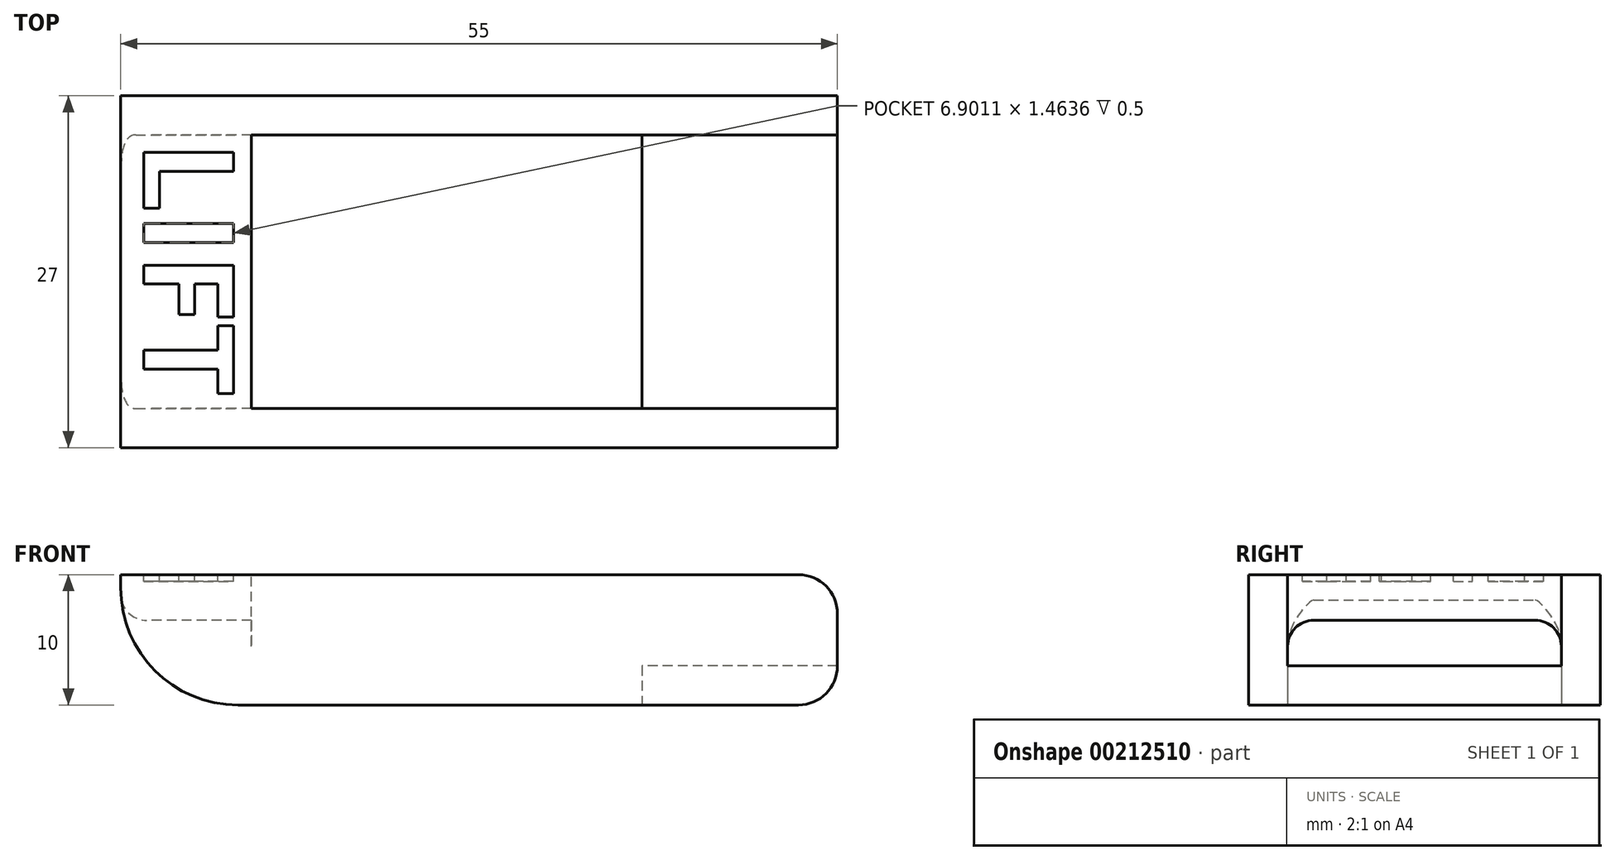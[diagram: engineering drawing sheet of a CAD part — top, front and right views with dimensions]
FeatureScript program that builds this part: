
annotation { "Feature Type Name" : "Feature", "Feature Type Description" : "" }
export const myFeature = defineFeature(function(context is Context, id is Id, definition is map)
    precondition{}
    {
        {
            var Q0;
            Q0=qCreatedBy(makeId("Top.planeOp"),FACE);
            var sketch = newSketch(context, id + "F0", { "sketchPlane" : qUnion([Q0])});
            skLineSegment(sketch, "E0.bottom", {"start": v(27.5, -10.5) * mm, "end": v(-27.5, -10.5) * mm});
            skLineSegment(sketch, "E0.top", {"start": v(27.5, 10.5) * mm, "end": v(-27.5, 10.5) * mm});
            skLineSegment(sketch, "E0.left", {"start": v(27.5, -10.5) * mm, "end": v(27.5, 10.5) * mm});
            skLineSegment(sketch, "E0.right", {"start": v(-27.5, -10.5) * mm, "end": v(-27.5, 10.5) * mm});
            skPoint(sketch, "E0.middle", {"position": v(0, 0) * mm});
            skLineSegment(sketch, "E1", {"start": v(12.5, 10.5) * mm, "end": v(12.5, -10.5) * mm});
            skLineSegment(sketch, "E2", {"start": v(27.5, 10.5) * mm, "end": v(27.5, 13.5) * mm});
            skLineSegment(sketch, "E3", {"start": v(27.5, 13.5) * mm, "end": v(-27.5, 13.5) * mm});
            skLineSegment(sketch, "E4", {"start": v(-27.5, 13.5) * mm, "end": v(-27.5, 10.5) * mm});
            skLineSegment(sketch, "E5", {"start": v(27.5, -10.5) * mm, "end": v(27.5, -13.5) * mm});
            skLineSegment(sketch, "E6", {"start": v(27.5, -13.5) * mm, "end": v(-27.5, -13.5) * mm});
            skLineSegment(sketch, "E7", {"start": v(-27.5, -13.5) * mm, "end": v(-27.5, -10.5) * mm});
            skLineSegment(sketch, "E8", {"start": v(-7.5, 10.5) * mm, "end": v(-7.5, -10.5) * mm});
            skSolve(sketch);
        }
        {
            var Q0;
            {var subQ0=sQuery(id+"F0.wireOp",EDGE,"E0.left");Q0=makeQuery(id+"F0.imprint","IMPRINT",FACE,{"disambiguationData":[TD([[makeQuery(id+"F0.imprint","IMPRINT",EDGE,{"derivedFrom":subQ0}),1.0]])]});}
            extrude(context, id + "F1", {"entities" : qUnion([Q0]), "depth" : 3 * mm});
        }
        {
            var Q0;
            {var subQ0=sQuery(id+"F0.wireOp",EDGE,"E5");Q0=makeQuery(id+"F0.imprint","IMPRINT",FACE,{"disambiguationData":[TD([[makeQuery(id+"F0.imprint","IMPRINT",EDGE,{"derivedFrom":subQ0}),-1.0]])]});}
            var Q1;
            {var subQ0=sQuery(id+"F0.wireOp",EDGE,"E2");Q1=makeQuery(id+"F0.imprint","IMPRINT",FACE,{"disambiguationData":[TD([[makeQuery(id+"F0.imprint","IMPRINT",EDGE,{"derivedFrom":subQ0}),1.0]])]});}
            extrude(context, id + "F2", {"entities" : qUnion([Q0, Q1]), "operationType" : NewBodyOperationType.ADD, "depth" : 10 * mm});
        }
        {
            var Q0;
            Q0=makeQuery(id+"F2.opExtrude","CAP_FACE",FACE,{"disambiguationData":[OSD([sQuery(id+"F0.wireOp",EDGE,"E0.top"),sQuery(id+"F0.wireOp",EDGE,"E2"),sQuery(id+"F0.wireOp",EDGE,"E3"),sQuery(id+"F0.wireOp",EDGE,"E4")])],"isStart":false});
            var sketch = newSketch(context, id + "F3", { "sketchPlane" : qUnion([Q0])});
            skLineSegment(sketch, "E9", {"start": v(-27.5, 13.5) * mm, "end": v(-27.5, -13.3) * mm});
            skLineSegment(sketch, "E10", {"start": v(-27.5, -13.3) * mm, "end": v(-17.46, -13.3) * mm});
            skLineSegment(sketch, "E11", {"start": v(-17.46, -13.3) * mm, "end": v(-17.46, 13.5) * mm});
            skLineSegment(sketch, "E12", {"start": v(-17.46, 13.5) * mm, "end": v(-27.5, 13.5) * mm});
            skSolve(sketch);
        }
        {
            var Q0;
            {var subQ3=sQuery(id+"F3.wireOp",EDGE,"E10");Q0=makeQuery(id+"F3.imprint","IMPRINT",FACE,{"disambiguationData":[TD([[makeQuery(id+"F3.imprint","IMPRINT",EDGE,{"derivedFrom":subQ3}),1.0]])]});}
            var Q1;
            {var subQ3=sQuery(id+"F3.wireOp",EDGE,"E12");Q1=makeQuery(id+"F3.imprint","IMPRINT",FACE,{"disambiguationData":[TD([[makeQuery(id+"F3.imprint","IMPRINT",EDGE,{"derivedFrom":subQ3}),1.0]])]});}
            extrude(context, id + "F4", {"entities" : qUnion([Q0, Q1]), "operationType" : NewBodyOperationType.ADD, "oppositeDirection" : true, "depth" : 3.5 * mm});
        }
        {
            var Q0;
            Q0=makeQuery(id+"F2.boolean.opBoolean","MERGE",EDGE,{"derivedFrom":[makeQuery(id+"F1.opExtrude","CAP_EDGE",EDGE,{"disambiguationData":[OSD([sQuery(id+"F0.wireOp",EDGE,"E0.left")])],"isStart":true}),makeQuery(id+"F2.opExtrude","CAP_EDGE",EDGE,{"disambiguationData":[OSD([sQuery(id+"F0.wireOp",EDGE,"E2")])],"isStart":true}),makeQuery(id+"F2.opExtrude","CAP_EDGE",EDGE,{"disambiguationData":[OSD([sQuery(id+"F0.wireOp",EDGE,"E5")])],"isStart":true})]});
            var Q1;
            Q1=makeQuery(id+"F2.opExtrude","CAP_EDGE",EDGE,{"disambiguationData":[OSD([sQuery(id+"F0.wireOp",EDGE,"E5")])],"isStart":false});
            var Q2;
            Q2=makeQuery(id+"F2.opExtrude","CAP_EDGE",EDGE,{"disambiguationData":[OSD([sQuery(id+"F0.wireOp",EDGE,"E2")])],"isStart":false});
            fillet(context, id + "F5", {"entities" : qUnion([Q0, Q1, Q2]), "radius" : 3 * mm, "tangentPropagation" : true, "allowEdgeOverflow" : false});
        }
        {
            var Q0;
            Q0=makeQuery(id+"F4.opExtrude","CAP_EDGE",EDGE,{"disambiguationData":[OSD([sQuery(id+"F3.wireOp",EDGE,"E9")])],"isStart":false});
            fillet(context, id + "F6", {"entities" : qUnion([Q0]), "radius" : 2 * mm, "tangentPropagation" : true, "allowEdgeOverflow" : false});
        }
        {
            var Q0;
            Q0=makeQuery(id+"F2.opExtrude","CAP_EDGE",EDGE,{"disambiguationData":[OSD([sQuery(id+"F0.wireOp",EDGE,"E4")])],"isStart":true});
            var Q1;
            Q1=makeQuery(id+"F2.opExtrude","CAP_EDGE",EDGE,{"disambiguationData":[OSD([sQuery(id+"F0.wireOp",EDGE,"E7")])],"isStart":true});
            fillet(context, id + "F7", {"entities" : qUnion([Q0, Q1]), "radius" : 9 * mm, "tangentPropagation" : true, "allowEdgeOverflow" : false});
        }
        {
            var Q0;
            Q0=makeQuery(id+"F4.boolean.opBoolean","INTERSECT",EDGE,{"derivedFrom":[makeQuery(id+"F2.opExtrude","SWEPT_FACE",FACE,{"disambiguationData":[OSD([sQuery(id+"F0.wireOp",EDGE,"E0.top")])]}),makeQuery(id+"F4.opExtrude","CAP_FACE",FACE,{"disambiguationData":[OSD([sQuery(id+"F3.wireOp",EDGE,"E9"),sQuery(id+"F3.wireOp",EDGE,"E10"),sQuery(id+"F3.wireOp",EDGE,"E11"),sQuery(id+"F3.wireOp",EDGE,"E12")])],"isStart":false})]});
            var Q1;
            Q1=makeQuery(id+"F4.boolean.opBoolean","INTERSECT",EDGE,{"derivedFrom":[makeQuery(id+"F2.opExtrude","SWEPT_FACE",FACE,{"disambiguationData":[OSD([sQuery(id+"F0.wireOp",EDGE,"E0.bottom")])]}),makeQuery(id+"F4.opExtrude","CAP_FACE",FACE,{"disambiguationData":[OSD([sQuery(id+"F3.wireOp",EDGE,"E9"),sQuery(id+"F3.wireOp",EDGE,"E10"),sQuery(id+"F3.wireOp",EDGE,"E11"),sQuery(id+"F3.wireOp",EDGE,"E12")])],"isStart":false})]});
            fillet(context, id + "F8", {"entities" : qUnion([Q0, Q1]), "radius" : 2 * mm, "tangentPropagation" : true, "allowEdgeOverflow" : false});
        }
        {
            var Q0;
            Q0=makeQuery(id+"F4.boolean.opBoolean","MERGE",FACE,{"derivedFrom":[makeQuery(id+"F2.opExtrude","CAP_FACE",FACE,{"disambiguationData":[OSD([sQuery(id+"F0.wireOp",EDGE,"E0.bottom"),sQuery(id+"F0.wireOp",EDGE,"E5"),sQuery(id+"F0.wireOp",EDGE,"E6"),sQuery(id+"F0.wireOp",EDGE,"E7")])],"isStart":false}),makeQuery(id+"F2.opExtrude","CAP_FACE",FACE,{"disambiguationData":[OSD([sQuery(id+"F0.wireOp",EDGE,"E0.top"),sQuery(id+"F0.wireOp",EDGE,"E2"),sQuery(id+"F0.wireOp",EDGE,"E3"),sQuery(id+"F0.wireOp",EDGE,"E4")])],"isStart":false}),makeQuery(id+"F4.opExtrude","CAP_FACE",FACE,{"disambiguationData":[OSD([sQuery(id+"F3.wireOp",EDGE,"E9"),sQuery(id+"F3.wireOp",EDGE,"E10"),sQuery(id+"F3.wireOp",EDGE,"E11"),sQuery(id+"F3.wireOp",EDGE,"E12")])],"isStart":true})]});
            var sketch = newSketch(context, id + "F9", { "sketchPlane" : qUnion([Q0])});
            skText(sketch, "E13", { "text": "LIFT", "fontName": "OpenSans-Bold.ttf"});
            const initialGuessF9  = {"E13": [-0.02574, 0.01002, 0, -1, 0.00696]};
            skSetInitialGuess(sketch, initialGuessF9);
            skSolve(sketch);
        }
        {
            var Q0;
            Q0 = qSketchRegion(id + "F9", true);
            extrude(context, id + "F10", {"entities" : qUnion([Q0]), "operationType" : NewBodyOperationType.REMOVE, "oppositeDirection" : true, "depth" : .5 * mm});
        }
    });
